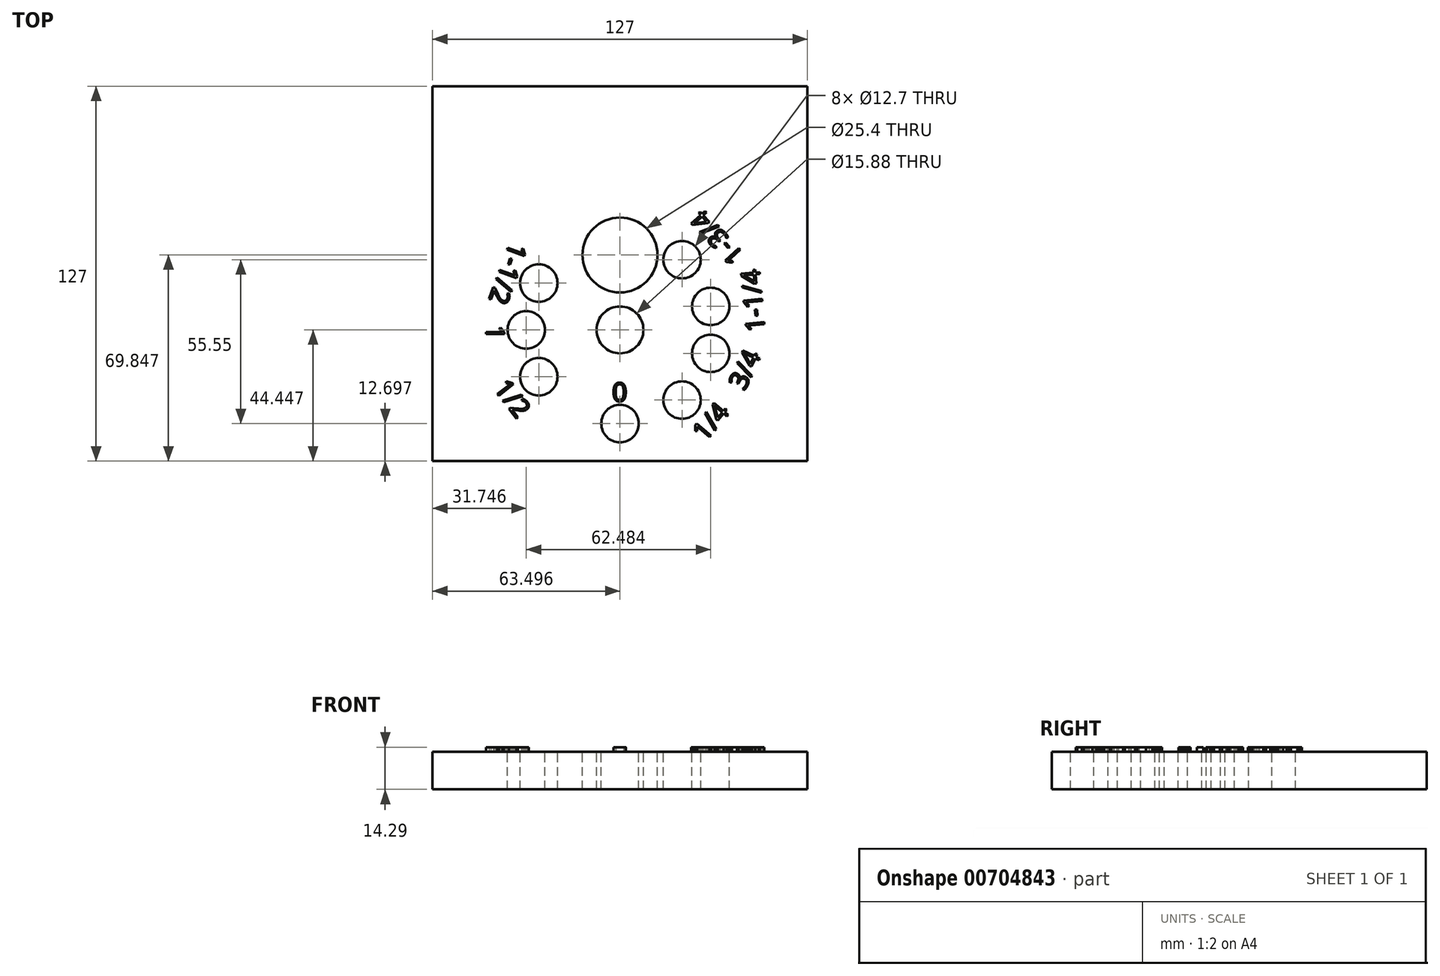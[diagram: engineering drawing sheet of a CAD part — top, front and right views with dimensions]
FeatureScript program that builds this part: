
annotation { "Feature Type Name" : "Feature", "Feature Type Description" : "" }
export const myFeature = defineFeature(function(context is Context, id is Id, definition is map)
    precondition{}
    {
        {
            var Q0;
            Q0=qCreatedBy(makeId("Top.planeOp"),FACE);
            var sketch = newSketch(context, id + "F0", { "sketchPlane" : qUnion([Q0])});
            skLineSegment(sketch, "E0.bottom", {"start": v(51.45, -36.98) * mm, "end": v(-75.55, -36.98) * mm});
            skLineSegment(sketch, "E0.top", {"start": v(51.45, 90.02) * mm, "end": v(-75.55, 90.02) * mm});
            skLineSegment(sketch, "E0.left", {"start": v(51.45, -36.98) * mm, "end": v(51.45, 90.02) * mm});
            skLineSegment(sketch, "E0.right", {"start": v(-75.55, -36.98) * mm, "end": v(-75.55, 90.02) * mm});
            skSolve(sketch);
        }
        {
            var Q0;
            Q0=makeQuery(id+"F0.imprint","IMPRINT",FACE,{"disambiguationData":[TD([[makeQuery(id+"F0.imprint","IMPRINT",EDGE,{"derivedFrom":sQuery(id+"F0.wireOp",EDGE,"E0.bottom")}),-1.0]])]});
            extrude(context, id + "F1", {"entities" : qUnion([Q0]), "depth" : 12.7 * mm, "offsetDistance" : 25.4 * mm});
        }
        {
            var Q0;
            Q0=makeQuery(id+"F1.opExtrude","CAP_FACE",FACE,{"disambiguationData":[OSD([sQuery(id+"F0.wireOp",EDGE,"E0.bottom"),sQuery(id+"F0.wireOp",EDGE,"E0.top"),sQuery(id+"F0.wireOp",EDGE,"E0.left"),sQuery(id+"F0.wireOp",EDGE,"E0.right")])],"isStart":false});
            var sketch = newSketch(context, id + "F2", { "sketchPlane" : qUnion([Q0])});
            skPoint(sketch, "E1", {"position": v(-12.05, -36.98) * mm});
            skPoint(sketch, "E2", {"position": v(-12.05, -24.28) * mm});
            skPoint(sketch, "E3", {"position": v(-39.56, -8.4) * mm});
            skPoint(sketch, "E4", {"position": v(-43.8, 7.47) * mm});
            skPoint(sketch, "E5", {"position": v(-39.56, 23.34) * mm});
            skPoint(sketch, "E6", {"position": v(-12.05, 7.47) * mm});
            skPoint(sketch, "E7", {"position": v(-12.05, 32.87) * mm});
            skPoint(sketch, "E8", {"position": v(8.95, 31.27) * mm});
            skPoint(sketch, "E9", {"position": v(8.95, -16.33) * mm});
            skPoint(sketch, "E10", {"position": v(18.68, 15.42) * mm});
            skPoint(sketch, "E11", {"position": v(18.68, -0.48) * mm});
            skSolve(sketch);
        }
        {
            var Q0;
            Q0=sQuery(id+"F2.wireOp",VERTEX,"E2");
            var Q1;
            Q1=sQuery(id+"F2.wireOp",VERTEX,"E3");
            var Q2;
            Q2=sQuery(id+"F2.wireOp",VERTEX,"E4");
            var Q3;
            Q3=sQuery(id+"F2.wireOp",VERTEX,"E5");
            var Q4;
            Q4=sQuery(id+"F2.wireOp",VERTEX,"E8");
            var Q5;
            Q5=sQuery(id+"F2.wireOp",VERTEX,"E10");
            var Q6;
            Q6=sQuery(id+"F2.wireOp",VERTEX,"E11");
            var Q7;
            Q7=sQuery(id+"F2.wireOp",VERTEX,"E9");
            var Q8;
            Q8=makeQuery(id+"F1.opExtrude","SWEPT_BODY",BODY,{"disambiguationData":[OSD([sQuery(id+"F0.wireOp",EDGE,"E0.bottom"),sQuery(id+"F0.wireOp",EDGE,"E0.top"),sQuery(id+"F0.wireOp",EDGE,"E0.left"),sQuery(id+"F0.wireOp",EDGE,"E0.right")])]});
            hole(context, id + "F3", {"style" : HoleStyle.SIMPLE, "endStyle" : HoleEndStyle.THROUGH, "holeDiameter" : 12.7 * mm, "majorDiameter" : 6.35 * mm, "isTappedThrough" : true, "tappedDepth" : 19.05 * mm, "tapClearance" : 3, "startFromSketch" : true, "locations" : qUnion([Q0, Q1, Q2, Q3, Q4, Q5, Q6, Q7]), "scope" : qUnion([Q8])});
        }
        {
            var Q0;
            Q0=sQuery(id+"F2.wireOp",VERTEX,"E7");
            var Q1;
            Q1=makeQuery(id+"F1.opExtrude","SWEPT_BODY",BODY,{"disambiguationData":[OSD([sQuery(id+"F0.wireOp",EDGE,"E0.bottom"),sQuery(id+"F0.wireOp",EDGE,"E0.top"),sQuery(id+"F0.wireOp",EDGE,"E0.left"),sQuery(id+"F0.wireOp",EDGE,"E0.right")])]});
            hole(context, id + "F4", {"style" : HoleStyle.SIMPLE, "endStyle" : HoleEndStyle.THROUGH, "holeDiameter" : 25.4 * mm, "majorDiameter" : 6.35 * mm, "isTappedThrough" : true, "tappedDepth" : 19.05 * mm, "tapClearance" : 3, "startFromSketch" : true, "locations" : qUnion([Q0]), "scope" : qUnion([Q1])});
        }
        {
            var Q0;
            Q0=sQuery(id+"F2.wireOp",VERTEX,"E6");
            var Q1;
            Q1=makeQuery(id+"F1.opExtrude","SWEPT_BODY",BODY,{"disambiguationData":[OSD([sQuery(id+"F0.wireOp",EDGE,"E0.bottom"),sQuery(id+"F0.wireOp",EDGE,"E0.top"),sQuery(id+"F0.wireOp",EDGE,"E0.left"),sQuery(id+"F0.wireOp",EDGE,"E0.right")])]});
            hole(context, id + "F5", {"style" : HoleStyle.SIMPLE, "endStyle" : HoleEndStyle.THROUGH, "holeDiameter" : 15.88 * mm, "majorDiameter" : 6.35 * mm, "isTappedThrough" : true, "tappedDepth" : 19.05 * mm, "tapClearance" : 3, "startFromSketch" : true, "locations" : qUnion([Q0]), "scope" : qUnion([Q1])});
        }
        {
            var Q0;
            Q0=makeQuery(id+"F2.imprint","IMPRINT",FACE,{"disambiguationData":[TD([[makeQuery(id+"F2.imprint","IMPRINT",EDGE,{"derivedFrom":makeQuery(id+"F1.opExtrude","CAP_EDGE",EDGE,{"disambiguationData":[OSD([sQuery(id+"F0.wireOp",EDGE,"E0.bottom")])],"isStart":false})}),-1.0]])]});
            var sketch = newSketch(context, id + "F6", { "sketchPlane" : qUnion([Q0])});
            skText(sketch, "E12", { "text": "1/4", "fontName": "OpenSans-Regular.ttf"});
            skText(sketch, "E13", { "text": "3/4\n", "fontName": "OpenSans-Regular.ttf"});
            skText(sketch, "E14", { "text": "1-1/4", "fontName": "OpenSans-Regular.ttf"});
            skText(sketch, "E15", { "text": "1-3/4", "fontName": "OpenSans-Regular.ttf"});
            skText(sketch, "E16", { "text": "0", "fontName": "OpenSans-Regular.ttf"});
            skText(sketch, "E17", { "text": "1/2", "fontName": "OpenSans-Regular.ttf"});
            skText(sketch, "E18", { "text": "1", "fontName": "OpenSans-Regular.ttf"});
            skText(sketch, "E19", { "text": "1-1/2", "fontName": "OpenSans-Regular.ttf"});
            const initialGuessF6  = {"E12": [0.01673, -0.03066, 0.64279, 0.76604, 0.00635], "E13": [0.03016, -0.0133, 0.42262, 0.9063, 0.00635], "E14": [0.03702, 0.00705, -0.08716, 0.9962, 0.00635], "E15": [0.03028, 0.03292, -0.67203, 0.74052, 0.00635], "E16": [-0.0147, -0.01677, 1, 0, 0.00635], "E17": [-0.05503, -0.01242, 0.61432, -0.78906, 0.00635], "E18": [-0.05747, 0.0091, 0, -1, 0.00635], "E19": [-0.0493, 0.0375, -0.34202, -0.9397, 0.00635]};
            skSetInitialGuess(sketch, initialGuessF6);
            skSolve(sketch);
        }
        {
            var Q0;
            Q0 = qSketchRegion(id + "F6", true);
            extrude(context, id + "F7", {"entities" : qUnion([Q0]), "operationType" : NewBodyOperationType.ADD, "depth" : 1.59 * mm, "offsetDistance" : 25.4 * mm});
        }
    });
